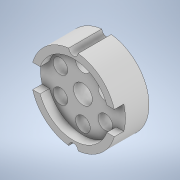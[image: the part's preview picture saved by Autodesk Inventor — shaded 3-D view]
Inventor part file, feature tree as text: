
AUTODESK INVENTOR PART (.ipt)
format: ipt  version: 2022 (Build 260153000, 153)  size: 167,424 bytes
history: native  units: mm
features: extrude x3, sketch x1
ambient origin geometry x8: Origin, YZ Plane, XZ Plane, XY Plane, X Axis, Y Axis, Z Axis, Center Point
bodies: Body1 (feature_tree)
feature tree (4):
  sketch  "草图3"  dims[d28=4.0mm d29=15.0mm d30=11.0mm d31=3.1mm d32=60.0mm d34=360.0deg d38=2.0mm d43=5.0mm d44=5.0mm d45=5.0mm d46=0.0mm d47=7.0mm d48=0.0mm d49=5.0mm d50=0.0mm d17=0.5mm d18=0.872665mm d19=0.5mm d20=0.872665mm]
  extrude  "拉伸4"  Depth=5.0mm
  extrude  "拉伸5"  Depth=5.0mm
  extrude  "拉伸6"  Depth=5.0mm
